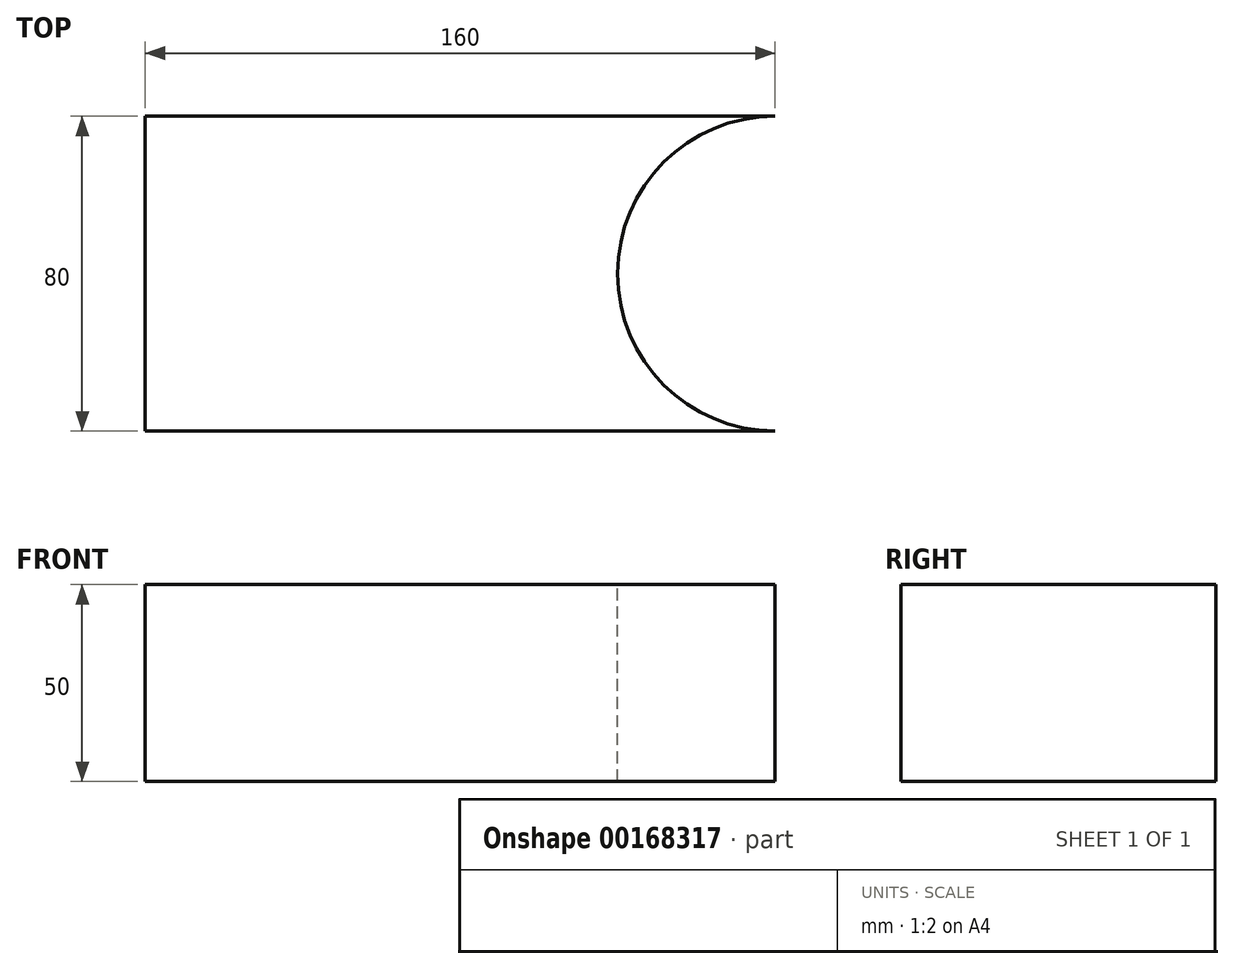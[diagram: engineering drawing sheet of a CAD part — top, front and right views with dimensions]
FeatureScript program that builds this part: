
annotation { "Feature Type Name" : "Feature", "Feature Type Description" : "" }
export const myFeature = defineFeature(function(context is Context, id is Id, definition is map)
    precondition{}
    {
        {
            var Q0;
            Q0=qCreatedBy(makeId("Right.planeOp"),FACE);
            var sketch = newSketch(context, id + "F0", { "sketchPlane" : qUnion([Q0])});
            skLineSegment(sketch, "E0.bottom", {"start": v(40, 25) * mm, "end": v(-40, 25) * mm});
            skLineSegment(sketch, "E0.top", {"start": v(40, -25) * mm, "end": v(-40, -25) * mm});
            skLineSegment(sketch, "E0.left", {"start": v(40, 25) * mm, "end": v(40, -25) * mm});
            skLineSegment(sketch, "E0.right", {"start": v(-40, 25) * mm, "end": v(-40, -25) * mm});
            skPoint(sketch, "E0.middle", {"position": v(0, 0) * mm});
            skSolve(sketch);
        }
        {
            var Q0;
            Q0=makeQuery(id+"F0.imprint","IMPRINT",FACE,{"disambiguationData":[TD([[makeQuery(id+"F0.imprint","IMPRINT",EDGE,{"derivedFrom":sQuery(id+"F0.wireOp",EDGE,"E0.bottom")}),1.0]])]});
            extrude(context, id + "F1", {"entities" : qUnion([Q0]), "depth" : 80 * mm});
        }
        {
            var Q0;
            Q0=makeQuery(id+"F1.opExtrude","CAP_FACE",FACE,{"disambiguationData":[OSD([sQuery(id+"F0.wireOp",EDGE,"E0.bottom"),sQuery(id+"F0.wireOp",EDGE,"E0.top"),sQuery(id+"F0.wireOp",EDGE,"E0.left"),sQuery(id+"F0.wireOp",EDGE,"E0.right")])],"isStart":true});
            extrude(context, id + "F2", {"entities" : qUnion([Q0]), "operationType" : NewBodyOperationType.ADD, "depth" : 80 * mm});
        }
        {
            var Q0;
            {var subQ0=sQuery(id+"F0.wireOp",EDGE,"E0.bottom");Q0=makeQuery(id+"F2.boolean.opBoolean","MERGE",FACE,{"derivedFrom":[makeQuery(id+"F1.opExtrude","SWEPT_FACE",FACE,{"disambiguationData":[OSD([subQ0])]}),makeQuery(id+"F2.opExtrude","SWEPT_FACE",FACE,{"disambiguationData":[OSD([subQ0])]})]});}
            var sketch = newSketch(context, id + "F3", { "sketchPlane" : qUnion([Q0])});
            skArc(sketch, "E1", {"start": v(80, 40) * mm, "mid": v(40, 0) * mm, "end": v(80, -40) * mm});
            skSolve(sketch);
        }
        {
            var Q0;
            Q0=makeQuery(id+"F3.imprint","IMPRINT",FACE,{"disambiguationData":[TD([[makeQuery(id+"F3.imprint","IMPRINT",EDGE,{"derivedFrom":sQuery(id+"F3.wireOp",EDGE,"E1")}),1.0]])]});
            var Q1;
            Q1 = qSketchRegion(id + "F3", true);
            extrude(context, id + "F4", {"entities" : qUnion([Q0, Q1]), "operationType" : NewBodyOperationType.REMOVE, "oppositeDirection" : true, "depth" : 50 * mm});
        }
    });
